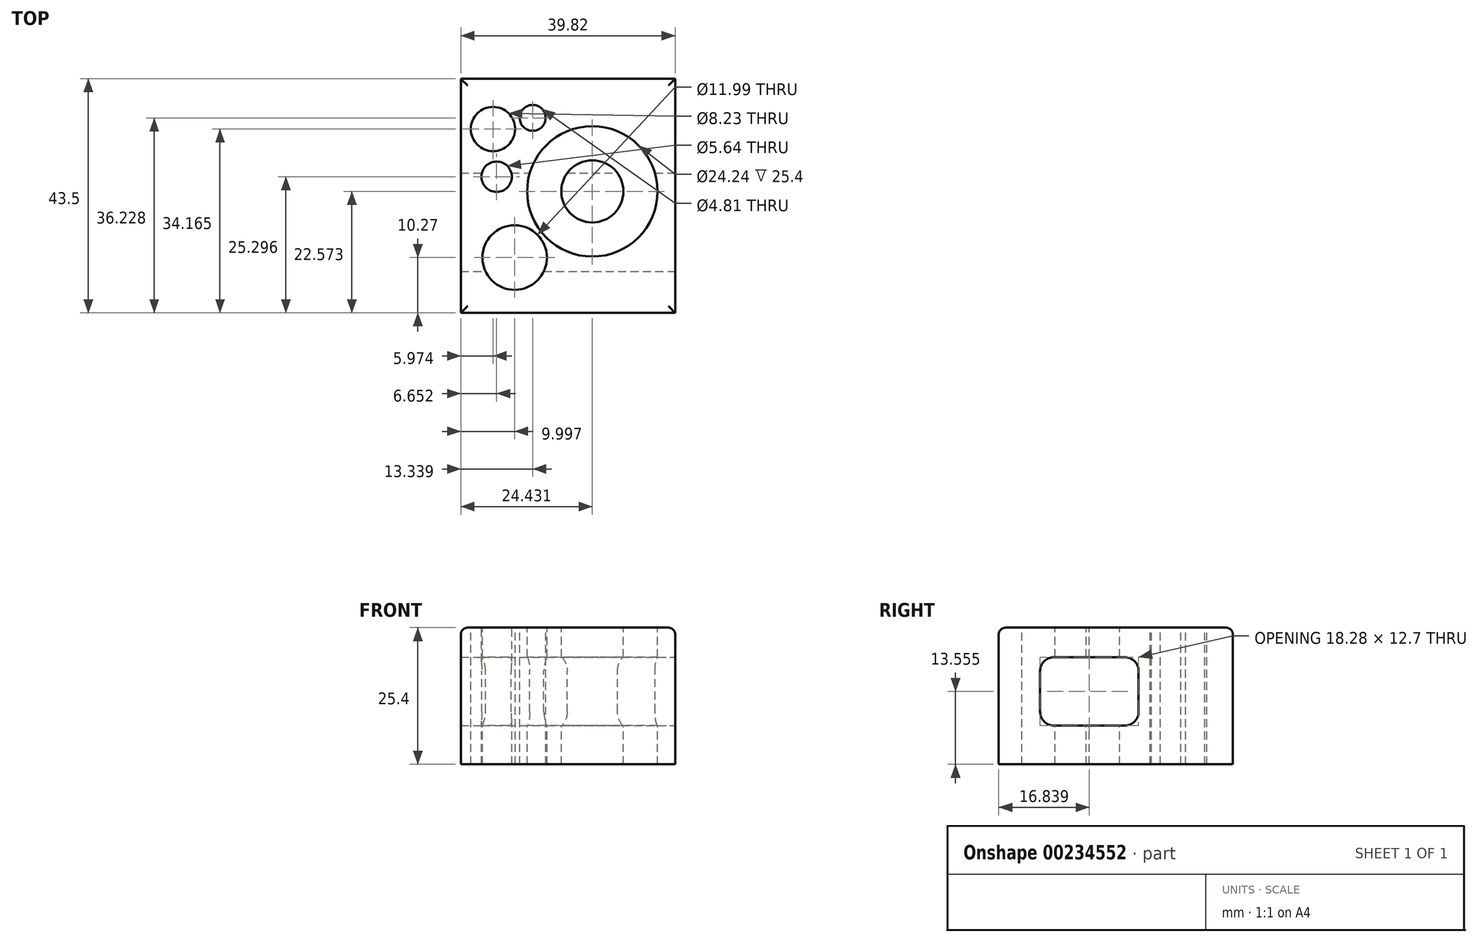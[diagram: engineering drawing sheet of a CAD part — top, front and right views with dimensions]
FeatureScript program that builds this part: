
annotation { "Feature Type Name" : "Feature", "Feature Type Description" : "" }
export const myFeature = defineFeature(function(context is Context, id is Id, definition is map)
    precondition{}
    {
        {
            var Q0;
            Q0=qCreatedBy(makeId("Top.planeOp"),FACE);
            var sketch = newSketch(context, id + "F0", { "sketchPlane" : qUnion([Q0])});
            skLineSegment(sketch, "E0.bottom", {"start": v(0, 0) * mm, "end": v(39.82, 0) * mm});
            skLineSegment(sketch, "E0.top", {"start": v(0, 43.5) * mm, "end": v(39.82, 43.5) * mm});
            skLineSegment(sketch, "E0.left", {"start": v(0, 0) * mm, "end": v(0, 43.5) * mm});
            skLineSegment(sketch, "E0.right", {"start": v(39.82, 0) * mm, "end": v(39.82, 43.5) * mm});
            skSolve(sketch);
        }
        {
            var Q0;
            Q0 = qSketchRegion(id + "F0", true);
            extrude(context, id + "F1", {"entities" : qUnion([Q0]), "depth" : 25.4 * mm});
        }
        {
            var Q0;
            Q0=makeQuery(id+"F1.opExtrude","CAP_FACE",FACE,{"disambiguationData":[OSD([sQuery(id+"F0.wireOp",EDGE,"E0.bottom"),sQuery(id+"F0.wireOp",EDGE,"E0.top"),sQuery(id+"F0.wireOp",EDGE,"E0.left"),sQuery(id+"F0.wireOp",EDGE,"E0.right")])],"isStart":false});
            var sketch = newSketch(context, id + "F2", { "sketchPlane" : qUnion([Q0])});
            skCircle(sketch, "E1", {"center": v(24.43, 22.57) * mm, "radius": 12.12 * mm});
            skPoint(sketch, "E1.first.point", {"position": v(12.83, 26.06) * mm});
            skPoint(sketch, "E1.second.point", {"position": v(32.76, 31.38) * mm});
            skPoint(sketch, "E1.third.point", {"position": v(25.77, 10.53) * mm});
            skCircle(sketch, "E2", {"center": v(10, 10.27) * mm, "radius": 6 * mm});
            skCircle(sketch, "E3", {"center": v(5.97, 34.16) * mm, "radius": 4.12 * mm});
            skCircle(sketch, "E4", {"center": v(6.65, 25.3) * mm, "radius": 2.82 * mm});
            skCircle(sketch, "E5", {"center": v(13.34, 36.23) * mm, "radius": 2.4 * mm});
            skCircle(sketch, "E6", {"center": v(24.43, 22.57) * mm, "radius": 5.77 * mm});
            skSolve(sketch);
        }
        {
            var Q0;
            Q0 = qSketchRegion(id + "F2", true);
            extrude(context, id + "F3", {"entities" : qUnion([Q0]), "operationType" : NewBodyOperationType.REMOVE, "endBound" : BoundingType.THROUGH_ALL, "oppositeDirection" : true, "depth" : 25.4 * mm});
        }
        {
            var Q0;
            Q0=makeQuery(id+"F1.opExtrude","CAP_EDGE",EDGE,{"disambiguationData":[OSD([sQuery(id+"F0.wireOp",EDGE,"E0.right")])],"isStart":false});
            var Q1;
            Q1=makeQuery(id+"F1.opExtrude","CAP_EDGE",EDGE,{"disambiguationData":[OSD([sQuery(id+"F0.wireOp",EDGE,"E0.left")])],"isStart":false});
            var Q2;
            Q2=makeQuery(id+"F1.opExtrude","CAP_EDGE",EDGE,{"disambiguationData":[OSD([sQuery(id+"F0.wireOp",EDGE,"E0.bottom")])],"isStart":false});
            var Q3;
            Q3=makeQuery(id+"F1.opExtrude","CAP_EDGE",EDGE,{"disambiguationData":[OSD([sQuery(id+"F0.wireOp",EDGE,"E0.top")])],"isStart":false});
            fillet(context, id + "F4", {"entities" : qUnion([Q0, Q1, Q2, Q3]), "radius" : 1.27 * mm, "tangentPropagation" : true, "allowEdgeOverflow" : false});
        }
        {
            var Q0;
            Q0=makeQuery(id+"F1.opExtrude","SWEPT_FACE",FACE,{"disambiguationData":[OSD([sQuery(id+"F0.wireOp",EDGE,"E0.right")])]});
            var sketch = newSketch(context, id + "F5", { "sketchPlane" : qUnion([Q0])});
            skLineSegment(sketch, "E7.bottom", {"start": v(10.24, 7.2) * mm, "end": v(23.44, 7.2) * mm});
            skLineSegment(sketch, "E7.top", {"start": v(10.24, 19.9) * mm, "end": v(23.44, 19.9) * mm});
            skLineSegment(sketch, "E7.left", {"start": v(7.7, 9.75) * mm, "end": v(7.7, 17.37) * mm});
            skLineSegment(sketch, "E7.right", {"start": v(25.98, 9.75) * mm, "end": v(25.98, 17.37) * mm});
            skPoint(sketch, "E8.visualSharp", {"position": v(25.98, 19.9) * mm});
            skArc(sketch, "E8.filletArc", {"start": v(25.98, 17.37) * mm, "mid": v(25.23, 19.16) * mm, "end": v(23.44, 19.9) * mm});
            skPoint(sketch, "E9.visualSharp", {"position": v(25.98, 7.2) * mm});
            skArc(sketch, "E9.filletArc", {"start": v(23.44, 7.2) * mm, "mid": v(25.23, 7.95) * mm, "end": v(25.98, 9.75) * mm});
            skPoint(sketch, "E10.visualSharp", {"position": v(7.7, 7.2) * mm});
            skArc(sketch, "E10.filletArc", {"start": v(7.7, 9.75) * mm, "mid": v(8.44, 7.95) * mm, "end": v(10.24, 7.2) * mm});
            skPoint(sketch, "E11.visualSharp", {"position": v(7.7, 19.9) * mm});
            skArc(sketch, "E11.filletArc", {"start": v(10.24, 19.9) * mm, "mid": v(8.44, 19.16) * mm, "end": v(7.7, 17.37) * mm});
            skSolve(sketch);
        }
        {
            var Q0;
            Q0 = qSketchRegion(id + "F5", true);
            extrude(context, id + "F6", {"entities" : qUnion([Q0]), "operationType" : NewBodyOperationType.REMOVE, "endBound" : BoundingType.THROUGH_ALL, "oppositeDirection" : true, "depth" : 25.4 * mm});
        }
    });
